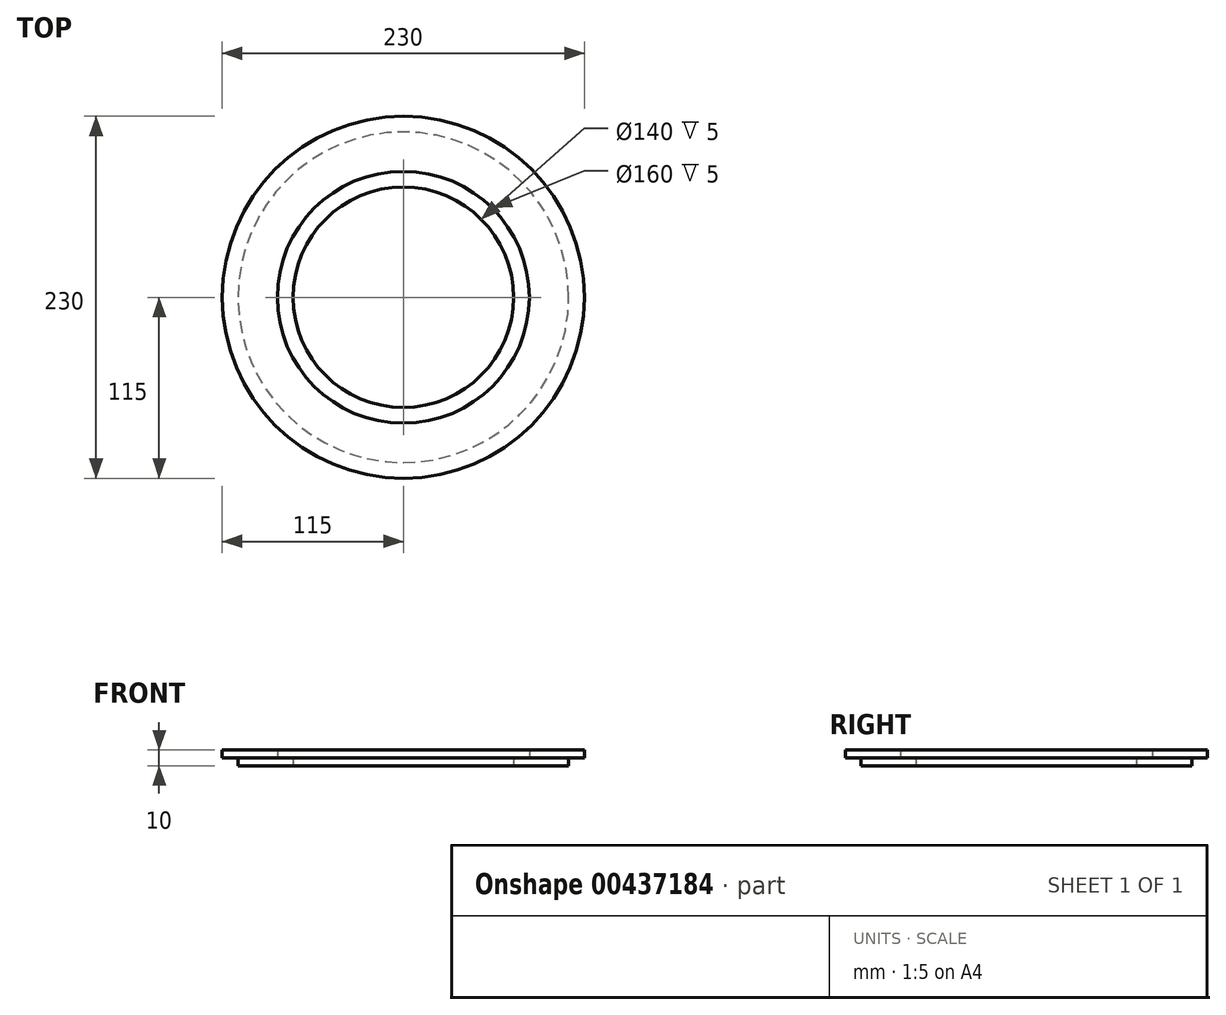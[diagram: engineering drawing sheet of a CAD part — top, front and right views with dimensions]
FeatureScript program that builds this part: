
annotation { "Feature Type Name" : "Feature", "Feature Type Description" : "" }
export const myFeature = defineFeature(function(context is Context, id is Id, definition is map)
    precondition{}
    {
        {
            var Q0;
            Q0=qCreatedBy(makeId("Front.planeOp"),FACE);
            var sketch = newSketch(context, id + "F0", { "sketchPlane" : qUnion([Q0])});
            skLineSegment(sketch, "E0", {"start": v(70, 0) * mm, "end": v(105, 0) * mm});
            skLineSegment(sketch, "E1", {"start": v(105, 0) * mm, "end": v(105, 5) * mm});
            skLineSegment(sketch, "E2", {"start": v(105, 5) * mm, "end": v(115, 5) * mm});
            skLineSegment(sketch, "E3", {"start": v(115, 5) * mm, "end": v(115, 10) * mm});
            skLineSegment(sketch, "E4", {"start": v(115, 10) * mm, "end": v(80, 10) * mm});
            skLineSegment(sketch, "E5", {"start": v(80, 10) * mm, "end": v(80, 5) * mm});
            skLineSegment(sketch, "E6", {"start": v(80, 5) * mm, "end": v(70, 5) * mm});
            skLineSegment(sketch, "E7", {"start": v(70, 5) * mm, "end": v(70, 0) * mm});
            skLineSegment(sketch, "E8", {"start": v(0, 0) * mm, "end": v(0, 115.63) * mm, "construction": true});
            skSolve(sketch);
        }
        {
            var Q0;
            Q0=makeQuery(id+"F0.imprint","IMPRINT",FACE,{"disambiguationData":[TD([[makeQuery(id+"F0.imprint","IMPRINT",EDGE,{"derivedFrom":sQuery(id+"F0.wireOp",EDGE,"E0")}),1.0]])]});
            var Q1;
            Q1=sQuery(id+"F0.wireOp",EDGE,"E8");
            var Q2;
            Q2=sQuery(id+"F0.wireOp",EDGE,"E8");
            revolve(context, id + "F1", {"entities" : qUnion([Q0]), "surfaceEntities" : qUnion([Q1]), "axis" : qUnion([Q2]), "revolveType" : RevolveType.FULL});
        }
    });
